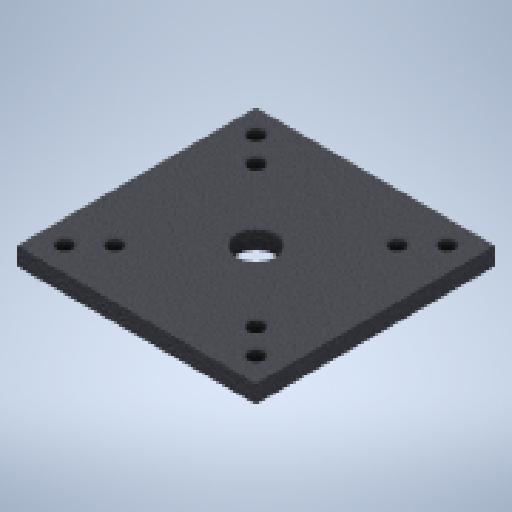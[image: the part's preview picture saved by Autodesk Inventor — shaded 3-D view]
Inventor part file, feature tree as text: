
AUTODESK INVENTOR PART (.ipt)
format: ipt  version: 2023 (Build 270158000, 158)  size: 284,672 bytes
history: native  units: mm
features: sketch x4, hole x3, other x1, extrude x1
ambient origin geometry x8: Origin, YZ Plane, XZ Plane, XY Plane, X Axis, Y Axis, Z Axis, Center Point
bodies: Body1 (feature_tree)
feature tree (9):
  other  "Sólido1"
  extrude  "Extrusão1"  Depth=80.0mm
  hole  "Furo1"  [1 undecoded]
  hole  "Furo2"  [1 undecoded]
  hole  "Furo3"  [1 undecoded]
  sketch  "Esboço1"  dims[d0=80.0mm d1=80.0mm]
  sketch  "Esboço2"  dims[d2=6.0mm d3=0.0mm d4=47.2mm]
  sketch  "Esboço3"  dims[d5=47.2mm d6=47.2mm]
  sketch  "Esboço4"  dims[d7=47.2mm d8=0.0mm d9=0.0mm d10=80.0mm d11=16.4mm d12=16.4mm d13=5.0mm d14=6.0mm d15=4.0mm d16=2.0mm d17=90.0deg d18=0.5mm d19=20.594885mm d20=8.0mm d21=8.0mm d22=8.0mm d23=8.0mm d24=8.0mm d25=8.0mm d26=8.0mm d27=8.0mm d28=5.0mm d29=6.0mm d30=4.0mm d31=2.0mm d32=90.0deg d33=8.0mm d34=20.594885mm d35=80.0mm d36=40.0mm d37=40.0mm d38=13.0mm d39=6.0mm d40=4.0mm d41=2.0mm d42=90.0deg d43=8.0mm d44=20.594885mm]
note: 3 required parameter values undecoded (feature->parameter linkage not recoverable at this tier; creation-order binding heuristic only, values carry confidence <= 0.55)
